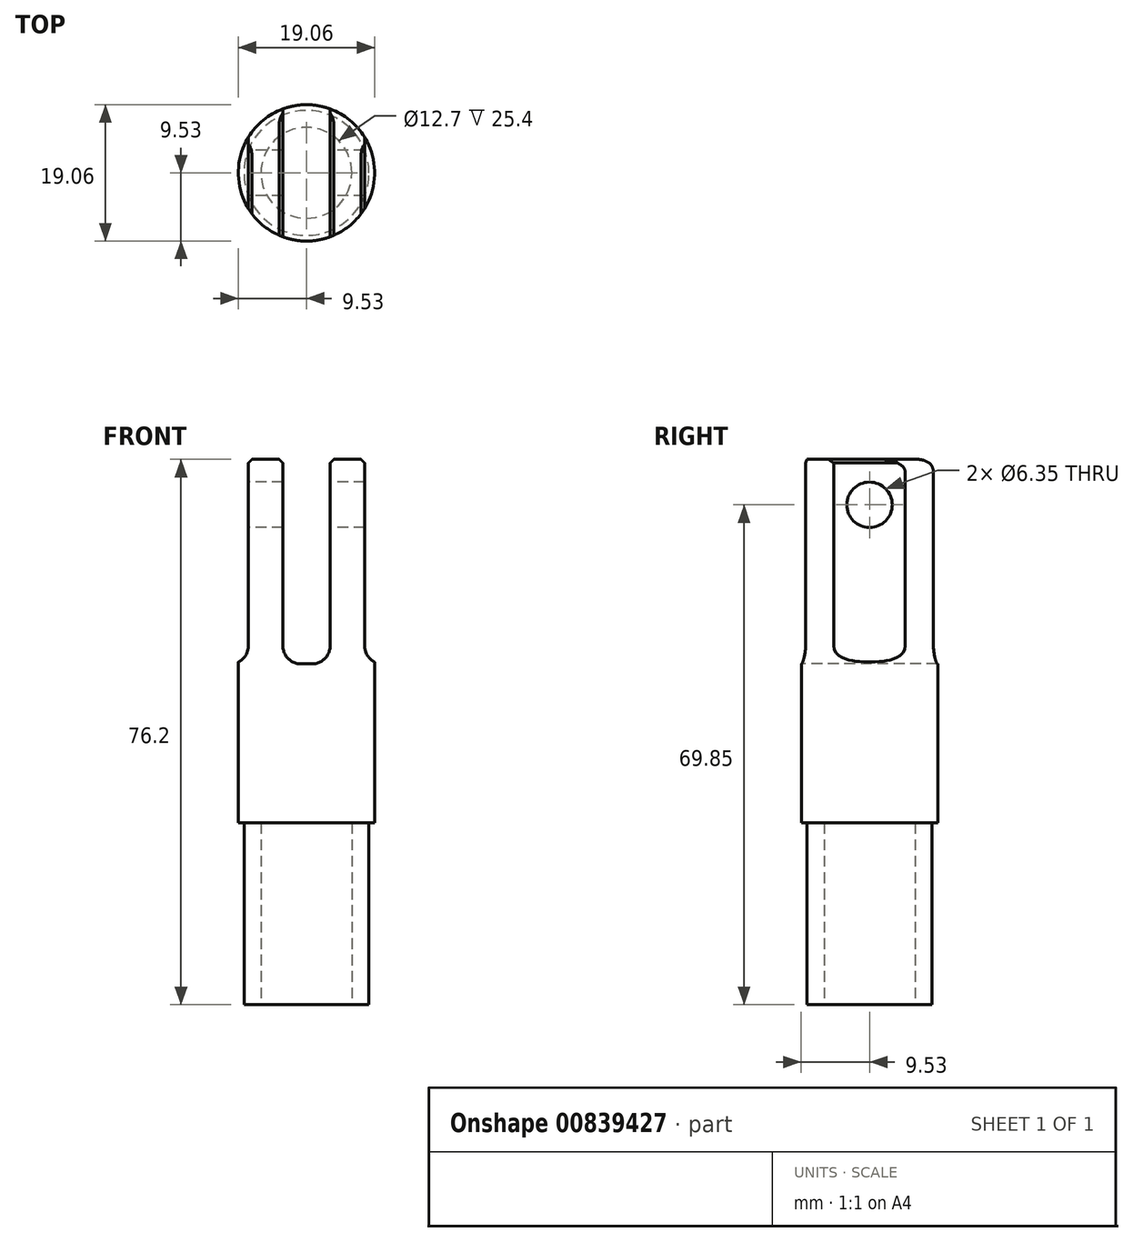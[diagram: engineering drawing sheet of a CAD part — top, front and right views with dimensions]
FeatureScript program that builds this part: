
annotation { "Feature Type Name" : "Feature", "Feature Type Description" : "" }
export const myFeature = defineFeature(function(context is Context, id is Id, definition is map)
    precondition{}
    {
        {
            var Q0;
            Q0=qCreatedBy(makeId("Top.planeOp"),FACE);
            var sketch = newSketch(context, id + "F0", { "sketchPlane" : qUnion([Q0])});
            skCircle(sketch, "E0", {"center": v(0, 0) * mm, "radius": 8.72 * mm});
            skSolve(sketch);
        }
        {
            var Q0;
            Q0 = qSketchRegion(id + "F0", true);
            extrude(context, id + "F1", {"entities" : qUnion([Q0]), "depth" : 25.4 * mm, "offsetDistance" : 25.4 * mm});
        }
        {
            var Q0;
            Q0=makeQuery(id+"F1.opExtrude","CAP_FACE",FACE,{"disambiguationData":[OSD([sQuery(id+"F0.wireOp",EDGE,"E0")])],"isStart":false});
            var sketch = newSketch(context, id + "F2", { "sketchPlane" : qUnion([Q0])});
            skCircle(sketch, "E1", {"center": v(0, 0) * mm, "radius": 9.53 * mm});
            skSolve(sketch);
        }
        {
            var Q0;
            Q0 = qSketchRegion(id + "F2", true);
            extrude(context, id + "F3", {"entities" : qUnion([Q0]), "operationType" : NewBodyOperationType.ADD, "depth" : 50.8 * mm, "offsetDistance" : 25.4 * mm});
        }
        {
            var Q0;
            Q0=qCreatedBy(makeId("Front.planeOp"),FACE);
            var sketch = newSketch(context, id + "F4", { "sketchPlane" : qUnion([Q0])});
            skLineSegment(sketch, "E2.bottom", {"start": v(3.3, 79.38) * mm, "end": v(-3.3, 79.38) * mm});
            skLineSegment(sketch, "E2.top", {"start": v(3.3, 47.62) * mm, "end": v(-3.3, 47.62) * mm});
            skLineSegment(sketch, "E2.left", {"start": v(3.3, 79.38) * mm, "end": v(3.3, 47.62) * mm});
            skLineSegment(sketch, "E2.right", {"start": v(-3.3, 79.38) * mm, "end": v(-3.3, 47.62) * mm});
            skPoint(sketch, "E2.middle", {"position": v(0, 63.5) * mm});
            skLineSegment(sketch, "E3.bottom", {"start": v(15.9, 85.12) * mm, "end": v(8.11, 85.12) * mm});
            skLineSegment(sketch, "E3.top", {"start": v(15.9, 47.62) * mm, "end": v(8.11, 47.62) * mm});
            skLineSegment(sketch, "E3.left", {"start": v(15.9, 85.12) * mm, "end": v(15.9, 47.62) * mm});
            skLineSegment(sketch, "E3.right", {"start": v(8.11, 85.12) * mm, "end": v(8.11, 47.62) * mm});
            skLineSegment(sketch, "E4.MirrorCS", {"start": v(-15.9, 85.12) * mm, "end": v(-8.11, 85.12) * mm});
            skLineSegment(sketch, "E5.MirrorCS", {"start": v(-8.11, 85.12) * mm, "end": v(-8.11, 47.62) * mm});
            skLineSegment(sketch, "E6.MirrorCS", {"start": v(-15.9, 85.12) * mm, "end": v(-15.9, 47.62) * mm});
            skLineSegment(sketch, "E7.MirrorCS", {"start": v(-15.9, 47.62) * mm, "end": v(-8.11, 47.62) * mm});
            skSolve(sketch);
        }
        {
            var Q0;
            Q0 = qSketchRegion(id + "F4", true);
            extrude(context, id + "F5", {"entities" : qUnion([Q0]), "operationType" : NewBodyOperationType.REMOVE, "oppositeDirection" : true, "depth" : 25.4 * mm, "offsetDistance" : 25.4 * mm, "hasSecondDirection" : true, "secondDirectionOppositeDirection" : false, "secondDirectionDepth" : 25.4 * mm});
        }
        {
            var Q0;
            Q0=makeQuery(id+"F5.boolean.opBoolean","COPY",EDGE,{"derivedFrom":makeQuery(id+"F5.opExtrude","SWEPT_EDGE",EDGE,{"disambiguationData":[OSD([sQuery(id+"F4.wireOp",EDGE,"E2.top"),sQuery(id+"F4.wireOp",EDGE,"E2.right")])]})});
            var Q1;
            Q1=makeQuery(id+"F5.boolean.opBoolean","COPY",EDGE,{"derivedFrom":makeQuery(id+"F5.opExtrude","SWEPT_EDGE",EDGE,{"disambiguationData":[OSD([sQuery(id+"F4.wireOp",EDGE,"E2.top"),sQuery(id+"F4.wireOp",EDGE,"E2.left")])]})});
            fillet(context, id + "F6", {"entities" : qUnion([Q0, Q1]), "tangentPropagation" : true, "radius" : 2.54 * mm, "defaultsChanged" : false, "vertexSettings" : [], "allowEdgeOverflow" : false});
        }
        {
            var Q0;
            Q0=makeQuery(id+"F5.boolean.opBoolean","INTERSECT",EDGE,{"derivedFrom":[makeQuery(id+"F3.opExtrude","CAP_FACE",FACE,{"disambiguationData":[OSD([sQuery(id+"F2.wireOp",EDGE,"E1")])],"isStart":false}),makeQuery(id+"F5.opExtrude","SWEPT_FACE",FACE,{"disambiguationData":[OSD([sQuery(id+"F4.wireOp",EDGE,"E2.left")])]})]});
            var Q1;
            Q1=makeQuery(id+"F5.boolean.opBoolean","INTERSECT",EDGE,{"derivedFrom":[makeQuery(id+"F3.opExtrude","CAP_FACE",FACE,{"disambiguationData":[OSD([sQuery(id+"F2.wireOp",EDGE,"E1")])],"isStart":false}),makeQuery(id+"F5.opExtrude","SWEPT_FACE",FACE,{"disambiguationData":[OSD([sQuery(id+"F4.wireOp",EDGE,"E2.right")])]})]});
            var Q2;
            Q2=makeQuery(id+"F5.boolean.opBoolean","INTERSECT",EDGE,{"derivedFrom":[makeQuery(id+"F3.opExtrude","CAP_FACE",FACE,{"disambiguationData":[OSD([sQuery(id+"F2.wireOp",EDGE,"E1")])],"isStart":false}),makeQuery(id+"F5.opExtrude","SWEPT_FACE",FACE,{"disambiguationData":[OSD([sQuery(id+"F4.wireOp",EDGE,"E5.MirrorCS")])]})]});
            var Q3;
            Q3=makeQuery(id+"F5.boolean.opBoolean","INTERSECT",EDGE,{"derivedFrom":[makeQuery(id+"F3.opExtrude","CAP_FACE",FACE,{"disambiguationData":[OSD([sQuery(id+"F2.wireOp",EDGE,"E1")])],"isStart":false}),makeQuery(id+"F5.opExtrude","SWEPT_FACE",FACE,{"disambiguationData":[OSD([sQuery(id+"F4.wireOp",EDGE,"E3.right")])]})]});
            chamfer(context, id + "F7", {"entities" : qUnion([Q0, Q1, Q2, Q3]), "width" : 0.5 * mm, "tangentPropagation" : true});
        }
        {
            var Q0;
            Q0=makeQuery(id+"F5.boolean.opBoolean","COPY",EDGE,{"derivedFrom":makeQuery(id+"F5.opExtrude","SWEPT_EDGE",EDGE,{"disambiguationData":[OSD([sQuery(id+"F4.wireOp",EDGE,"E3.top"),sQuery(id+"F4.wireOp",EDGE,"E3.right")])]})});
            var Q1;
            Q1=makeQuery(id+"F5.boolean.opBoolean","COPY",EDGE,{"derivedFrom":makeQuery(id+"F5.opExtrude","SWEPT_EDGE",EDGE,{"disambiguationData":[OSD([sQuery(id+"F4.wireOp",EDGE,"E5.MirrorCS"),sQuery(id+"F4.wireOp",EDGE,"E7.MirrorCS")])]})});
            fillet(context, id + "F8", {"entities" : qUnion([Q0, Q1]), "tangentPropagation" : true, "radius" : 2.54 * mm, "defaultsChanged" : true, "vertexSettings" : [], "allowEdgeOverflow" : false});
        }
        {
            var Q0;
            Q0=makeQuery(id+"F5.boolean.opBoolean","COPY",FACE,{"derivedFrom":makeQuery(id+"F5.opExtrude","SWEPT_FACE",FACE,{"disambiguationData":[OSD([sQuery(id+"F4.wireOp",EDGE,"E5.MirrorCS")])]})});
            var sketch = newSketch(context, id + "F9", { "sketchPlane" : qUnion([Q0])});
            skCircle(sketch, "E8", {"center": v(0, 69.85) * mm, "radius": 3.18 * mm});
            skSolve(sketch);
        }
        {
            var Q0;
            Q0 = qSketchRegion(id + "F9", true);
            extrude(context, id + "F10", {"entities" : qUnion([Q0]), "operationType" : NewBodyOperationType.REMOVE, "oppositeDirection" : true, "depth" : 25.4 * mm, "offsetDistance" : 25.4 * mm, "hasSecondDirection" : true, "secondDirectionOppositeDirection" : false, "secondDirectionDepth" : 25.4 * mm});
        }
        {
            var Q0;
            {var subQ0=sQuery(id+"F2.wireOp",EDGE,"E1");Q0=makeQuery(id+"F5.boolean.opBoolean","SPLIT",EDGE,{"disambiguationData":[TD([makeQuery(id+"F3.opExtrude","SWEPT_FACE",FACE,{"disambiguationData":[OSD([subQ0])]}),makeQuery(id+"F3.opExtrude","CAP_FACE",FACE,{"disambiguationData":[OSD([subQ0])],"isStart":false}),makeQuery(id+"F5.opExtrude","SWEPT_FACE",FACE,{"disambiguationData":[OSD([sQuery(id+"F4.wireOp",EDGE,"E2.left")])]}),makeQuery(id+"F5.opExtrude","SWEPT_FACE",FACE,{"disambiguationData":[OSD([sQuery(id+"F4.wireOp",EDGE,"E3.right")])]})]),OD(1.0)],"derivedFrom":makeQuery(id+"F3.opExtrude","CAP_EDGE",EDGE,{"disambiguationData":[OSD([subQ0])],"isStart":false})});}
            var Q1;
            {var subQ0=sQuery(id+"F2.wireOp",EDGE,"E1");Q1=makeQuery(id+"F5.boolean.opBoolean","SPLIT",EDGE,{"disambiguationData":[TD([makeQuery(id+"F3.opExtrude","SWEPT_FACE",FACE,{"disambiguationData":[OSD([subQ0])]}),makeQuery(id+"F3.opExtrude","CAP_FACE",FACE,{"disambiguationData":[OSD([subQ0])],"isStart":false}),makeQuery(id+"F5.opExtrude","SWEPT_FACE",FACE,{"disambiguationData":[OSD([sQuery(id+"F4.wireOp",EDGE,"E2.right")])]}),makeQuery(id+"F5.opExtrude","SWEPT_FACE",FACE,{"disambiguationData":[OSD([sQuery(id+"F4.wireOp",EDGE,"E5.MirrorCS")])]})]),OD(1.0)],"derivedFrom":makeQuery(id+"F3.opExtrude","CAP_EDGE",EDGE,{"disambiguationData":[OSD([subQ0])],"isStart":false})});}
            fillet(context, id + "F11", {"entities" : qUnion([Q0, Q1]), "tangentPropagation" : true, "radius" : 1.78 * mm, "defaultsChanged" : true, "vertexSettings" : [], "allowEdgeOverflow" : false});
        }
        {
            var Q0;
            Q0=makeQuery(id+"F1.opExtrude","CAP_FACE",FACE,{"disambiguationData":[OSD([sQuery(id+"F0.wireOp",EDGE,"E0")])],"isStart":true});
            var sketch = newSketch(context, id + "F12", { "sketchPlane" : qUnion([Q0])});
            skCircle(sketch, "E9", {"center": v(0, 0) * mm, "radius": 6.35 * mm});
            skSolve(sketch);
        }
        {
            var Q0;
            Q0 = qSketchRegion(id + "F12", true);
            extrude(context, id + "F13", {"entities" : qUnion([Q0]), "operationType" : NewBodyOperationType.REMOVE, "oppositeDirection" : true, "depth" : 25.4 * mm, "offsetDistance" : 25.4 * mm});
        }
    });
